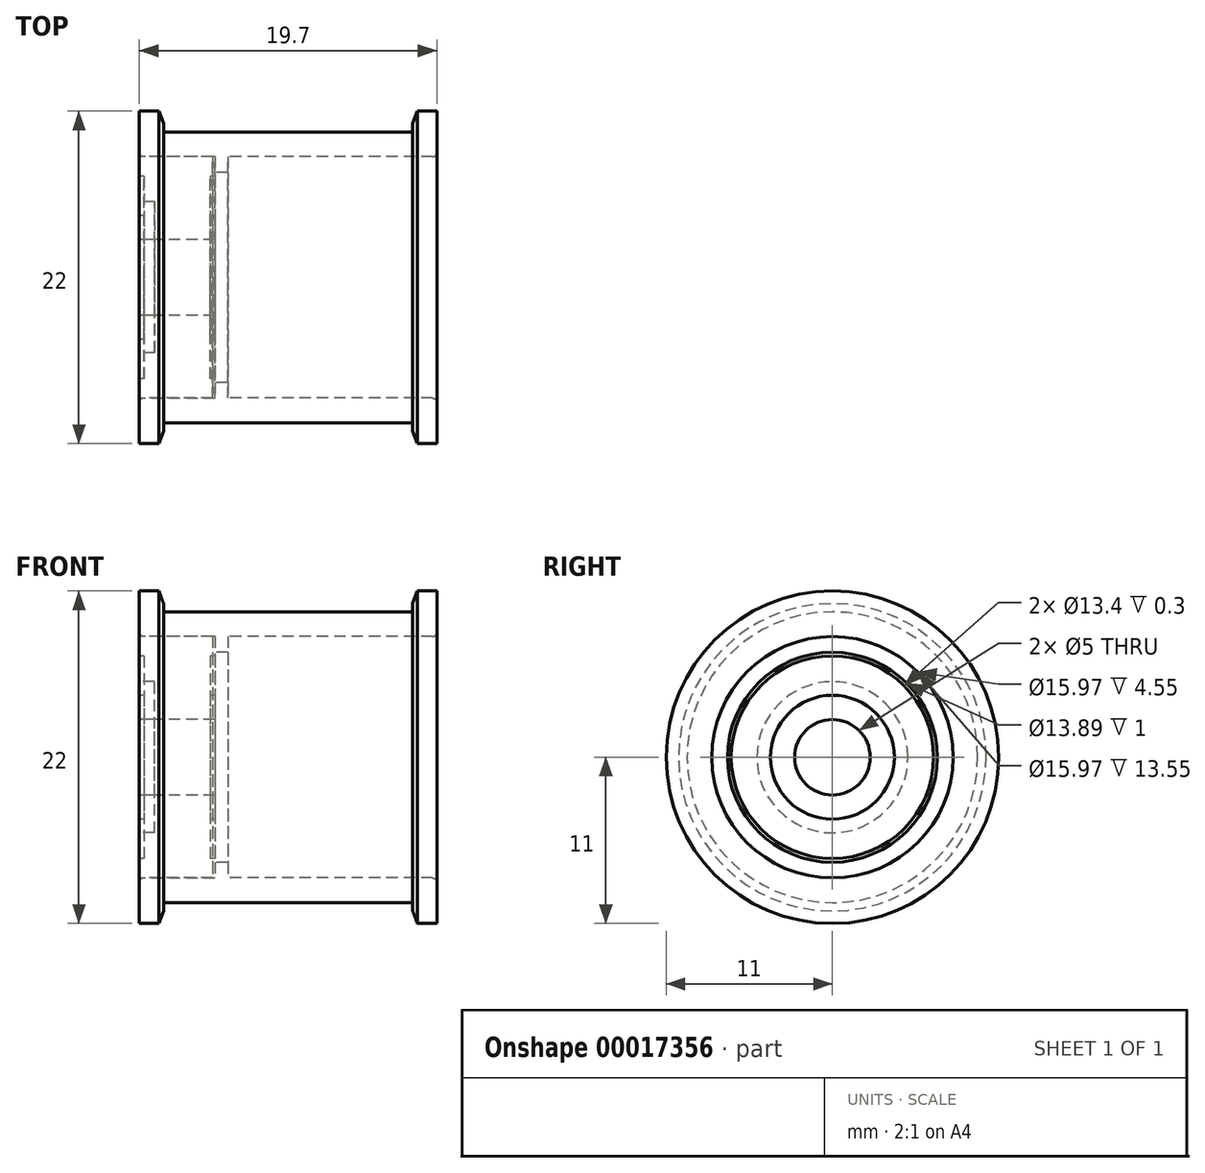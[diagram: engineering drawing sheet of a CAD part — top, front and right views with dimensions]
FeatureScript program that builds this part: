
annotation { "Feature Type Name" : "Feature", "Feature Type Description" : "" }
export const myFeature = defineFeature(function(context is Context, id is Id, definition is map)
    precondition{}
    {
        {
            var Q0;
            Q0=qCreatedBy(makeId("Front.planeOp"),FACE);
            var sketch = newSketch(context, id + "F0", { "sketchPlane" : qUnion([Q0])});
            skLineSegment(sketch, "E0", {"start": v(0, 11) * mm, "end": v(0, 7.99) * mm});
            skLineSegment(sketch, "E1", {"start": v(0, 7.99) * mm, "end": v(4.85, 7.99) * mm});
            skLineSegment(sketch, "E2", {"start": v(4.85, 7.99) * mm, "end": v(4.85, 6.95) * mm});
            skLineSegment(sketch, "E3", {"start": v(4.85, 6.95) * mm, "end": v(5.85, 6.95) * mm});
            skLineSegment(sketch, "E4", {"start": v(5.85, 6.94) * mm, "end": v(5.85, 7.99) * mm});
            skLineSegment(sketch, "E5", {"start": v(5.85, 7.99) * mm, "end": v(19.7, 7.99) * mm});
            skLineSegment(sketch, "E6", {"start": v(19.7, 7.99) * mm, "end": v(19.7, 11) * mm});
            skLineSegment(sketch, "E7", {"start": v(19.7, 11) * mm, "end": v(18.1, 11) * mm});
            skLineSegment(sketch, "E8", {"start": v(18.1, 11) * mm, "end": v(18.1, 9.62) * mm});
            skLineSegment(sketch, "E9", {"start": v(18.1, 9.62) * mm, "end": v(1.6, 9.62) * mm});
            skLineSegment(sketch, "E10", {"start": v(1.6, 9.62) * mm, "end": v(1.6, 11) * mm});
            skLineSegment(sketch, "E11", {"start": v(1.6, 11) * mm, "end": v(0, 11) * mm});
            skLineSegment(sketch, "E12", {"start": v(2.55, 0) * mm, "end": v(13, 0) * mm, "construction": true});
            skSolve(sketch);
        }
        {
            var Q0;
            Q0=makeQuery(id+"F0.imprint","IMPRINT",FACE,{"disambiguationData":[TD([[makeQuery(id+"F0.imprint","IMPRINT",EDGE,{"derivedFrom":sQuery(id+"F0.wireOp",EDGE,"E0")}),1.0]])]});
            var Q1;
            Q1=sQuery(id+"F0.wireOp",EDGE,"E12");
            revolve(context, id + "F1", {"entities" : qUnion([Q0]), "axis" : qUnion([Q1]), "revolveType" : RevolveType.FULL});
        }
        {
            var Q0;
            Q0=makeQuery(id+"F1.opRevolve","SWEPT_EDGE",EDGE,{"disambiguationData":[OSD([sQuery(id+"F0.wireOp",EDGE,"E0"),sQuery(id+"F0.wireOp",EDGE,"E1")])]});
            var Q1;
            Q1=makeQuery(id+"F1.opRevolve","SWEPT_EDGE",EDGE,{"disambiguationData":[OSD([sQuery(id+"F0.wireOp",EDGE,"E5"),sQuery(id+"F0.wireOp",EDGE,"E6")])]});
            fillet(context, id + "F2", {"entities" : qUnion([Q0, Q1]), "radius" : 0.3 * mm, "allowEdgeOverflow" : false});
        }
        {
            var Q0;
            Q0=qCreatedBy(makeId("Right.planeOp"),FACE);
            var sketch = newSketch(context, id + "F3", { "sketchPlane" : qUnion([Q0])});
            skCircle(sketch, "E13", {"center": v(0, 0) * mm, "radius": 2.5 * mm});
            skCircle(sketch, "E14", {"center": v(0, 0) * mm, "radius": 5 * mm});
            skSolve(sketch);
        }
        {
            var Q0;
            Q0=makeQuery(id+"F3.imprint","IMPRINT",FACE,{"disambiguationData":[TD([[makeQuery(id+"F3.imprint","IMPRINT",EDGE,{"derivedFrom":sQuery(id+"F3.wireOp",EDGE,"E13")}),-1.0]])]});
            extrude(context, id + "F4", {"entities" : qUnion([Q0]), "depth" : 1 * mm});
        }
        {
            var Q0;
            Q0=qCreatedBy(makeId("Front.planeOp"),FACE);
            var sketch = newSketch(context, id + "F5", { "sketchPlane" : qUnion([Q0])});
            skLineSegment(sketch, "E15", {"start": v(0, 8) * mm, "end": v(0, 6.7) * mm});
            skLineSegment(sketch, "E16", {"start": v(0, 6.7) * mm, "end": v(0.3, 6.7) * mm});
            skLineSegment(sketch, "E17", {"start": v(0.3, 6.7) * mm, "end": v(0.3, 4.1) * mm});
            skLineSegment(sketch, "E18", {"start": v(0.3, 4.1) * mm, "end": v(0, 4.1) * mm});
            skLineSegment(sketch, "E19", {"start": v(0, 4.1) * mm, "end": v(0, 2.5) * mm});
            skLineSegment(sketch, "E20", {"start": v(0, 2.5) * mm, "end": v(5, 2.5) * mm});
            skLineSegment(sketch, "E21", {"start": v(5, 2.5) * mm, "end": v(5, 4.1) * mm});
            skLineSegment(sketch, "E22", {"start": v(5, 4.1) * mm, "end": v(4.7, 4.1) * mm});
            skLineSegment(sketch, "E23", {"start": v(4.7, 4.1) * mm, "end": v(4.7, 6.7) * mm});
            skLineSegment(sketch, "E24", {"start": v(4.7, 6.7) * mm, "end": v(5, 6.7) * mm});
            skLineSegment(sketch, "E25", {"start": v(5, 6.7) * mm, "end": v(5, 8) * mm});
            skLineSegment(sketch, "E26", {"start": v(5, 8) * mm, "end": v(0, 8) * mm});
            skLineSegment(sketch, "E27", {"start": v(0, 0) * mm, "end": v(7.53, 0) * mm, "construction": true});
            skSolve(sketch);
        }
        {
            var Q0;
            Q0 = qSketchRegion(id + "F5", true);
            var Q1;
            Q1=sQuery(id+"F5.wireOp",EDGE,"E27");
            revolve(context, id + "F6", {"entities" : qUnion([Q0]), "axis" : qUnion([Q1]), "revolveType" : RevolveType.FULL});
        }
        {
            var Q0;
            Q0=makeQuery(id+"F1.opRevolve","SWEPT_EDGE",EDGE,{"disambiguationData":[OSD([sQuery(id+"F0.wireOp",EDGE,"E10"),sQuery(id+"F0.wireOp",EDGE,"E11")])]});
            chamfer(context, id + "F7", {"entities" : qUnion([Q0]), "chamferType" : ChamferType.OFFSET_ANGLE, "width" : 0.3 * mm, "oppositeDirection" : false, "angle" : 70 * degree, "tangentPropagation" : true});
        }
        {
            var Q0;
            Q0=makeQuery(id+"F1.opRevolve","SWEPT_EDGE",EDGE,{"disambiguationData":[OSD([sQuery(id+"F0.wireOp",EDGE,"E7"),sQuery(id+"F0.wireOp",EDGE,"E8")])]});
            chamfer(context, id + "F8", {"entities" : qUnion([Q0]), "chamferType" : ChamferType.OFFSET_ANGLE, "width" : 0.3 * mm, "oppositeDirection" : true, "angle" : 70 * degree, "tangentPropagation" : true});
        }
    });
